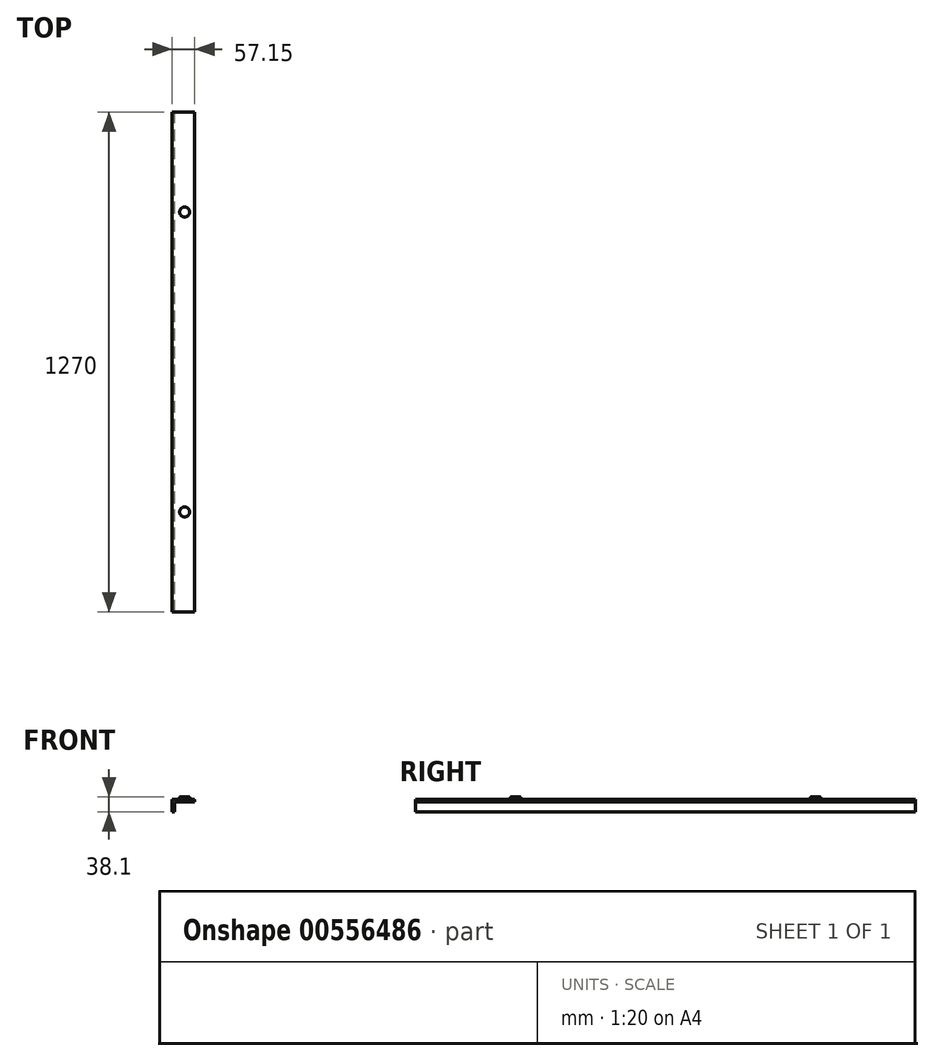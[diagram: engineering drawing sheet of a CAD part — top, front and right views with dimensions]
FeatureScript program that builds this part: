
annotation { "Feature Type Name" : "Feature", "Feature Type Description" : "" }
export const myFeature = defineFeature(function(context is Context, id is Id, definition is map)
    precondition{}
    {
        {
            var Q0;
            Q0=qCreatedBy(makeId("Front.planeOp"),FACE);
            var sketch = newSketch(context, id + "F0", { "sketchPlane" : qUnion([Q0])});
            skLineSegment(sketch, "E0", {"start": v(0, 0) * mm, "end": v(-50.8, 0) * mm});
            skLineSegment(sketch, "E1", {"start": v(-50.8, 0) * mm, "end": v(-50.8, -25.4) * mm});
            skLineSegment(sketch, "E2.0", {"start": v(-57.15, 6.35) * mm, "end": v(-57.15, -25.4) * mm});
            skLineSegment(sketch, "E2.1", {"start": v(0, 6.35) * mm, "end": v(-57.15, 6.35) * mm});
            skLineSegment(sketch, "E3", {"start": v(0, 6.35) * mm, "end": v(0, 0) * mm});
            skLineSegment(sketch, "E4", {"start": v(-50.8, -25.4) * mm, "end": v(-57.15, -25.4) * mm});
            skSolve(sketch);
        }
        {
            var Q0;
            Q0=makeQuery(id+"F0.imprint","IMPRINT",FACE,{"disambiguationData":[TD([[makeQuery(id+"F0.imprint","IMPRINT",EDGE,{"derivedFrom":sQuery(id+"F0.wireOp",EDGE,"E0")}),-1.0]])]});
            extrude(context, id + "F1", {"entities" : qUnion([Q0]), "endBound" : BoundingType.SYMMETRIC, "depth" : 1270 * mm, "offsetDistance" : 25.4 * mm});
        }
        {
            var Q0;
            Q0=qCreatedBy(makeId("Top.planeOp"),FACE);
            var sketch = newSketch(context, id + "F2", { "sketchPlane" : qUnion([Q0])});
            skCircle(sketch, "E5", {"center": v(-25.4, 381) * mm, "radius": 12.7 * mm});
            skCircle(sketch, "E6", {"center": v(-25.4, -381) * mm, "radius": 12.7 * mm});
            skSolve(sketch);
        }
        {
            var Q0;
            Q0 = qSketchRegion(id + "F2", true);
            extrude(context, id + "F3", {"entities" : qUnion([Q0]), "operationType" : NewBodyOperationType.ADD, "depth" : 12.7 * mm, "offsetDistance" : 25.4 * mm});
        }
        {
            var Q0;
            Q0=makeQuery(id+"F3.boolean.opBoolean","INTERSECT",EDGE,{"derivedFrom":[makeQuery(id+"F1.opExtrude","SWEPT_FACE",FACE,{"disambiguationData":[OSD([sQuery(id+"F0.wireOp",EDGE,"E2.1")])]}),makeQuery(id+"F3.opExtrude","SWEPT_FACE",FACE,{"disambiguationData":[OSD([sQuery(id+"F2.wireOp",EDGE,"E5")])]})]});
            fillet(context, id + "F4", {"entities" : qUnion([Q0]), "radius" : 7.62 * mm, "tangentPropagation" : true, "allowEdgeOverflow" : false});
        }
        {
            var Q0;
            Q0=makeQuery(id+"F3.boolean.opBoolean","INTERSECT",EDGE,{"derivedFrom":[makeQuery(id+"F1.opExtrude","SWEPT_FACE",FACE,{"disambiguationData":[OSD([sQuery(id+"F0.wireOp",EDGE,"E2.1")])]}),makeQuery(id+"F3.opExtrude","SWEPT_FACE",FACE,{"disambiguationData":[OSD([sQuery(id+"F2.wireOp",EDGE,"E6")])]})]});
            fillet(context, id + "F5", {"entities" : qUnion([Q0]), "radius" : 7.62 * mm, "tangentPropagation" : true, "allowEdgeOverflow" : false});
        }
    });
